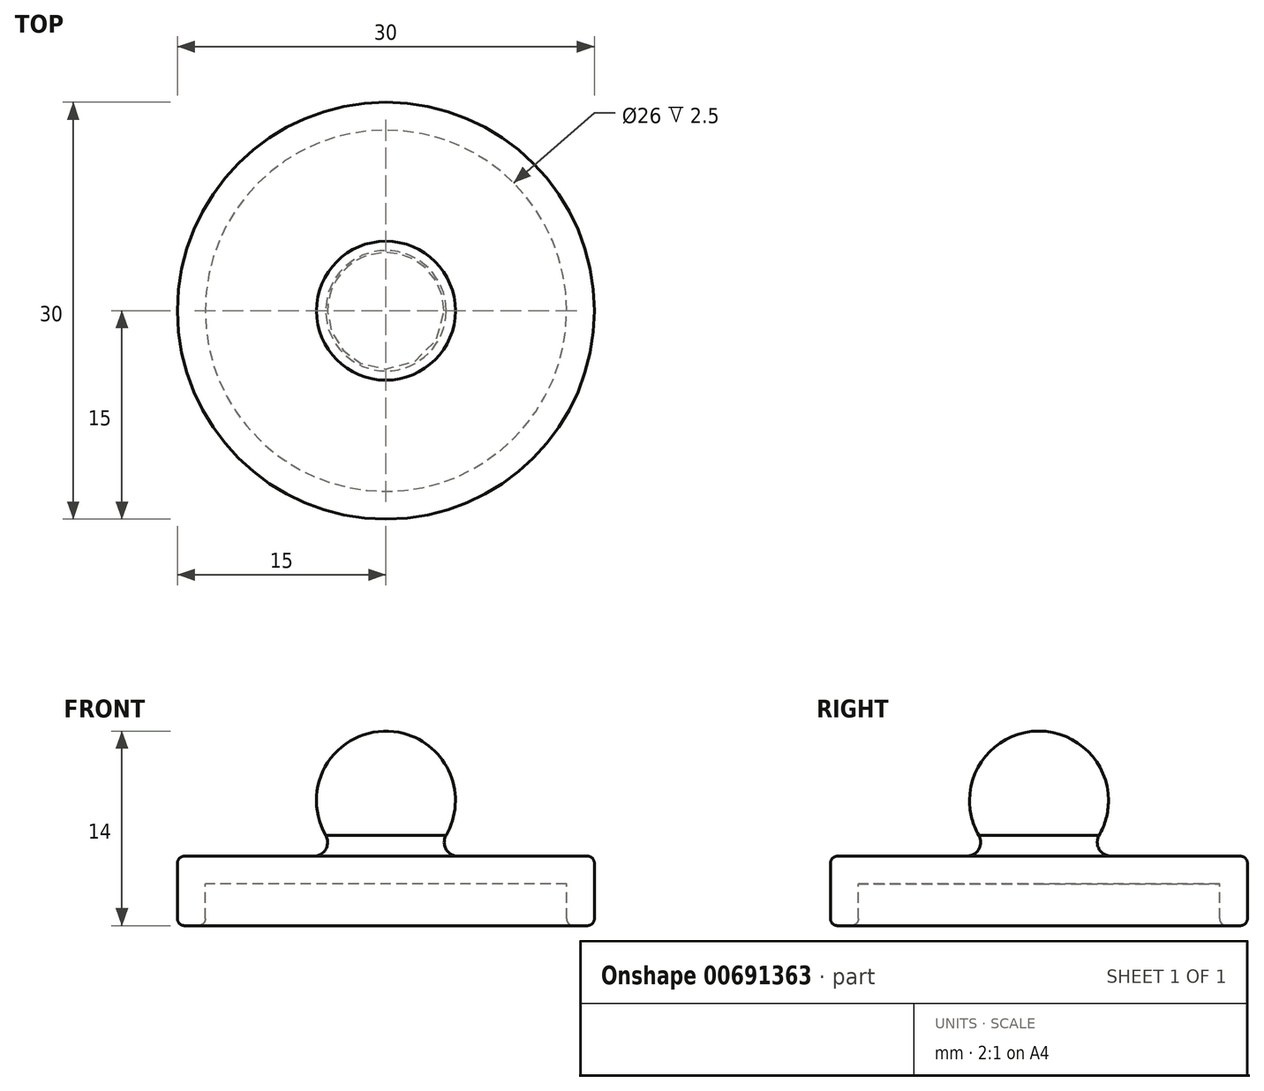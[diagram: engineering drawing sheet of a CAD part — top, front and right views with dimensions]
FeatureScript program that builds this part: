
annotation { "Feature Type Name" : "Feature", "Feature Type Description" : "" }
export const myFeature = defineFeature(function(context is Context, id is Id, definition is map)
    precondition{}
    {
        {
            var Q0;
            Q0=qCreatedBy(makeId("Top.planeOp"),FACE);
            var sketch = newSketch(context, id + "F0", { "sketchPlane" : qUnion([Q0])});
            skArc(sketch, "E0", {"start": v(0, -5) * mm, "mid": v(5, 0) * mm, "end": v(0, 5) * mm});
            skLineSegment(sketch, "E1", {"start": v(0, -5) * mm, "end": v(0, 5) * mm, "construction": true});
            skLineSegment(sketch, "E2", {"start": v(0, 5) * mm, "end": v(0, -5) * mm});
            skSolve(sketch);
        }
        {
            var Q0;
            Q0=makeQuery(id+"F0.imprint","IMPRINT",FACE,{"disambiguationData":[TD([[makeQuery(id+"F0.imprint","IMPRINT",EDGE,{"derivedFrom":sQuery(id+"F0.wireOp",EDGE,"E0")}),1.0]])]});
            var Q1;
            Q1=sQuery(id+"F0.wireOp",EDGE,"E2");
            revolve(context, id + "F1", {"entities" : qUnion([Q0]), "axis" : qUnion([Q1]), "revolveType" : RevolveType.FULL});
        }
        {
            var Q0;
            Q0=qCreatedBy(makeId("Top.planeOp"),FACE);
            cPlane(context, id + "F2", {"entities" : qUnion([Q0]), "cplaneType" : CPlaneType.OFFSET, "offset" : 4 * mm, "oppositeDirection" : true, "width" : 150 * mm, "height" : 150 * mm});
        }
        {
            var Q0;
            Q0=qCreatedBy(id+"F2.planeOp",FACE);
            var sketch = newSketch(context, id + "F3", { "sketchPlane" : qUnion([Q0])});
            skCircle(sketch, "E3", {"center": v(0, 0) * mm, "radius": 13 * mm});
            skCircle(sketch, "E4", {"center": v(0, 0) * mm, "radius": 15 * mm});
            skSolve(sketch);
        }
        {
            var Q0;
            Q0=makeQuery(id+"F3.imprint","IMPRINT",FACE,{"disambiguationData":[TD([[makeQuery(id+"F3.imprint","IMPRINT",EDGE,{"derivedFrom":sQuery(id+"F3.wireOp",EDGE,"E3")}),1.0]])]});
            extrude(context, id + "F4", {"entities" : qUnion([Q0]), "operationType" : NewBodyOperationType.ADD, "oppositeDirection" : true, "depth" : 2 * mm, "offsetDistance" : 25 * mm});
        }
        {
            var Q0;
            Q0=makeQuery(id+"F3.imprint","IMPRINT",FACE,{"disambiguationData":[TD([[makeQuery(id+"F3.imprint","IMPRINT",EDGE,{"derivedFrom":sQuery(id+"F3.wireOp",EDGE,"E3")}),-1.0]])]});
            extrude(context, id + "F5", {"entities" : qUnion([Q0]), "operationType" : NewBodyOperationType.ADD, "oppositeDirection" : true, "depth" : (2 + 3) * mm, "offsetDistance" : 25 * mm});
        }
        {
            var Q0;
            Q0=makeQuery(id+"F4.boolean.opBoolean","INTERSECT",EDGE,{"derivedFrom":[makeQuery(id+"F1.opRevolve","SWEPT_FACE",FACE,{"disambiguationData":[OSD([sQuery(id+"F0.wireOp",EDGE,"E0")])]}),makeQuery(id+"F4.opExtrude","CAP_FACE",FACE,{"disambiguationData":[OSD([sQuery(id+"F3.wireOp",EDGE,"E3")])],"isStart":true})]});
            fillet(context, id + "F6", {"entities" : qUnion([Q0]), "radius" : 1 * mm, "tangentPropagation" : true, "allowEdgeOverflow" : false});
        }
        {
            var Q0;
            Q0=makeQuery(id+"F5.opExtrude","CAP_EDGE",EDGE,{"disambiguationData":[OSD([sQuery(id+"F3.wireOp",EDGE,"E4")])],"isStart":true});
            var Q1;
            Q1=makeQuery(id+"F5.opExtrude","CAP_EDGE",EDGE,{"disambiguationData":[OSD([sQuery(id+"F3.wireOp",EDGE,"E3")])],"isStart":false});
            var Q2;
            Q2=makeQuery(id+"F5.opExtrude","CAP_EDGE",EDGE,{"disambiguationData":[OSD([sQuery(id+"F3.wireOp",EDGE,"E4")])],"isStart":false});
            var Q3;
            Q3=makeQuery(id+"F4.opExtrude","CAP_EDGE",EDGE,{"disambiguationData":[OSD([sQuery(id+"F3.wireOp",EDGE,"E3")])],"isStart":false});
            fillet(context, id + "F7", {"entities" : qUnion([Q0, Q1, Q2, Q3]), "radius" : 0.5 * mm, "tangentPropagation" : true, "allowEdgeOverflow" : false});
        }
    });
